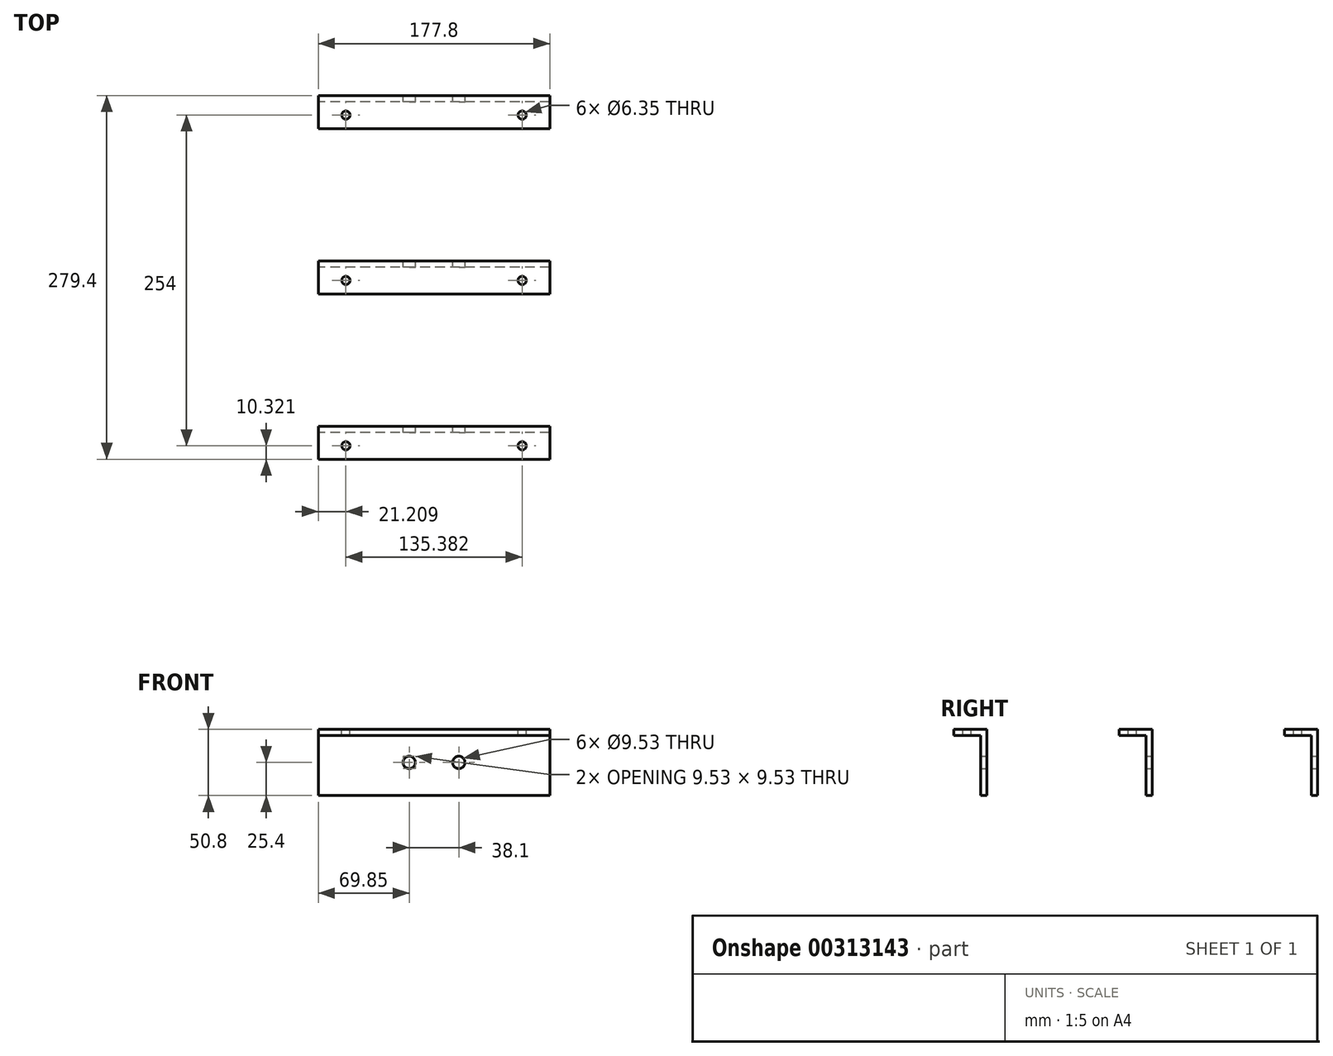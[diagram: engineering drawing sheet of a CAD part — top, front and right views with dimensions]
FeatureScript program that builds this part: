
annotation { "Feature Type Name" : "Feature", "Feature Type Description" : "" }
export const myFeature = defineFeature(function(context is Context, id is Id, definition is map)
    precondition{}
    {
        {
            var Q0;
            Q0=qCreatedBy(makeId("Right.planeOp"),FACE);
            var sketch = newSketch(context, id + "F0", { "sketchPlane" : qUnion([Q0])});
            skLineSegment(sketch, "E0", {"start": v(0, 0) * mm, "end": v(0, 46.04) * mm});
            skLineSegment(sketch, "E1", {"start": v(0, 46.04) * mm, "end": v(-20.64, 46.04) * mm});
            skLineSegment(sketch, "E2", {"start": v(-20.64, 46.04) * mm, "end": v(-20.64, 50.8) * mm});
            skLineSegment(sketch, "E3", {"start": v(-20.64, 50.8) * mm, "end": v(4.76, 50.8) * mm});
            skLineSegment(sketch, "E4", {"start": v(4.76, 50.8) * mm, "end": v(4.76, 0) * mm});
            skLineSegment(sketch, "E5", {"start": v(4.76, 0) * mm, "end": v(0, 0) * mm});
            skLineSegment(sketch, "E6.1.0.0", {"start": v(127, 46.04) * mm, "end": v(106.36, 46.04) * mm});
            skLineSegment(sketch, "E6.1.0.1", {"start": v(127, 0) * mm, "end": v(127, 46.04) * mm});
            skLineSegment(sketch, "E6.1.0.2", {"start": v(106.36, 50.8) * mm, "end": v(131.76, 50.8) * mm});
            skLineSegment(sketch, "E6.1.0.3", {"start": v(131.76, 50.8) * mm, "end": v(131.76, 0) * mm});
            skLineSegment(sketch, "E6.1.0.4", {"start": v(106.36, 46.04) * mm, "end": v(106.36, 50.8) * mm});
            skLineSegment(sketch, "E6.1.0.5", {"start": v(131.76, 0) * mm, "end": v(127, 0) * mm});
            skLineSegment(sketch, "E6.2.0.0", {"start": v(254, 46.04) * mm, "end": v(233.36, 46.04) * mm});
            skLineSegment(sketch, "E6.2.0.1", {"start": v(254, 0) * mm, "end": v(254, 46.04) * mm});
            skLineSegment(sketch, "E6.2.0.2", {"start": v(233.36, 50.8) * mm, "end": v(258.76, 50.8) * mm});
            skLineSegment(sketch, "E6.2.0.3", {"start": v(258.76, 50.8) * mm, "end": v(258.76, 0) * mm});
            skLineSegment(sketch, "E6.2.0.4", {"start": v(233.36, 46.04) * mm, "end": v(233.36, 50.8) * mm});
            skLineSegment(sketch, "E6.2.0.5", {"start": v(258.76, 0) * mm, "end": v(254, 0) * mm});
            skLineSegment(sketch, "E6.direction1", {"start": v(0, 0) * mm, "end": v(127, 0) * mm, "construction": true});
            skSolve(sketch);
        }
        {
            var Q0;
            Q0=qSketchRegion(id+"F0",true);
            extrude(context, id + "F1", {"entities" : qUnion([Q0]), "endBound" : BoundingType.SYMMETRIC, "depth" : 177.8 * mm, "offsetDistance" : 25.4 * mm});
        }
        {
            var Q0;
            Q0=makeQuery(id+"F1.opExtrude","SWEPT_FACE",FACE,{"disambiguationData":[OSD([sQuery(id+"F0.wireOp",EDGE,"E6.2.0.3")])]});
            var sketch = newSketch(context, id + "F2", { "sketchPlane" : qUnion([Q0])});
            skCircle(sketch, "E7", {"center": v(-19.05, 25.4) * mm, "radius": 4.76 * mm});
            skPoint(sketch, "E7.centerSnap0", {"position": v(-88.9, 25.4) * mm});
            skCircle(sketch, "E8", {"center": v(19.05, 25.4) * mm, "radius": 4.76 * mm});
            skLineSegment(sketch, "E9", {"start": v(-19.05, 25.4) * mm, "end": v(19.05, 25.4) * mm, "construction": true});
            skPoint(sketch, "E10", {"position": v(0, 25.4) * mm});
            skSolve(sketch);
        }
        {
            var Q0;
            Q0 = qSketchRegion(id + "F2", true);
            extrude(context, id + "F3", {"entities" : qUnion([Q0]), "operationType" : NewBodyOperationType.REMOVE, "endBound" : BoundingType.THROUGH_ALL, "oppositeDirection" : true, "depth" : 25.4 * mm});
        }
        {
            var Q0;
            Q0=makeQuery(id+"F1.opExtrude","SWEPT_FACE",FACE,{"disambiguationData":[OSD([sQuery(id+"F0.wireOp",EDGE,"E6.2.0.2")])]});
            var sketch = newSketch(context, id + "F4", { "sketchPlane" : qUnion([Q0])});
            skCircle(sketch, "E11", {"center": v(-67.7, 243.68) * mm, "radius": 3.18 * mm});
            skPoint(sketch, "E11.centerSnap0", {"position": v(-88.9, 246.06) * mm});
            skCircle(sketch, "E12.0.1.0", {"center": v(-67.7, 116.68) * mm, "radius": 3.18 * mm});
            skCircle(sketch, "E12.0.2.0", {"center": v(-67.7, -10.32) * mm, "radius": 3.18 * mm});
            skCircle(sketch, "E12.1.0.0", {"center": v(67.7, 243.68) * mm, "radius": 3.18 * mm});
            skCircle(sketch, "E12.1.1.0", {"center": v(67.7, 116.68) * mm, "radius": 3.18 * mm});
            skCircle(sketch, "E12.1.2.0", {"center": v(67.7, -10.32) * mm, "radius": 3.18 * mm});
            skLineSegment(sketch, "E12.direction1", {"start": v(-67.7, 243.68) * mm, "end": v(67.7, 243.68) * mm, "construction": true});
            skLineSegment(sketch, "E12.direction2", {"start": v(-67.7, 243.68) * mm, "end": v(-67.7, 116.68) * mm, "construction": true});
            skSolve(sketch);
        }
        {
            var Q0;
            Q0 = qSketchRegion(id + "F4", true);
            extrude(context, id + "F5", {"entities" : qUnion([Q0]), "operationType" : NewBodyOperationType.REMOVE, "endBound" : BoundingType.THROUGH_ALL, "oppositeDirection" : true, "depth" : 25.4 * mm});
        }
    });
